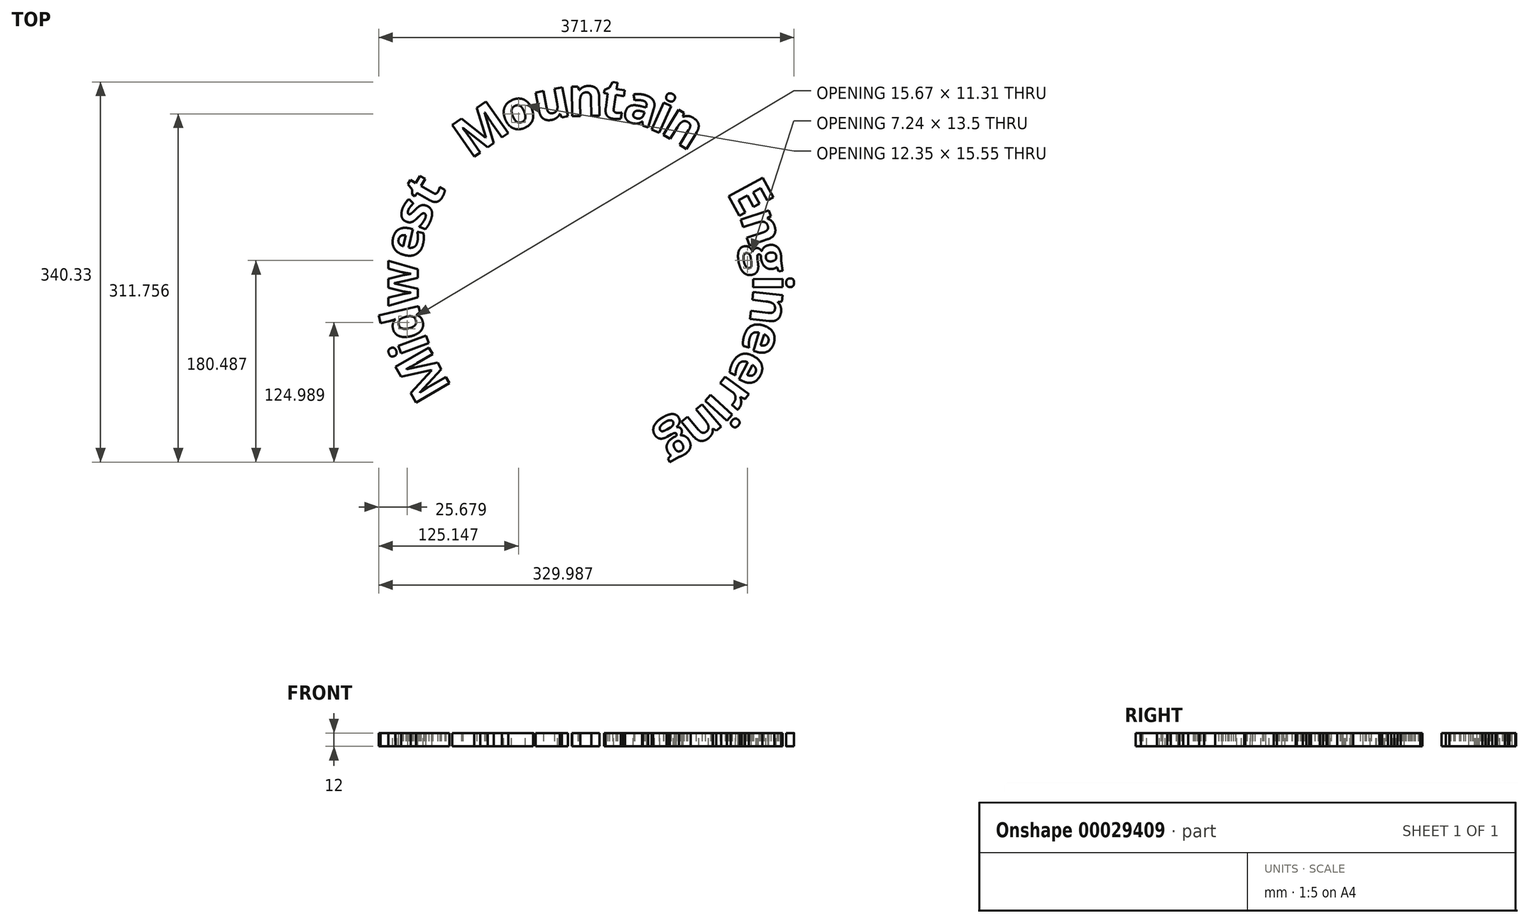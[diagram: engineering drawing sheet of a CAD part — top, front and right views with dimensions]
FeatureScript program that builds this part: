
annotation { "Feature Type Name" : "Feature", "Feature Type Description" : "" }
export const myFeature = defineFeature(function(context is Context, id is Id, definition is map)
    precondition{}
    {
        {
            var Q0;
            Q0=qCreatedBy(makeId("Top.planeOp"),FACE);
            var sketch = newSketch(context, id + "F0", { "sketchPlane" : qUnion([Q0])});
            skCircle(sketch, "E0", {"center": v(0, 0) * mm, "radius": 150 * mm, "construction": true});
            skLineSegment(sketch, "E1", {"start": v(0, 0) * mm, "end": v(-129.76, -75.25) * mm, "construction": true});
            skLineSegment(sketch, "E2", {"start": v(0, 0) * mm, "end": v(-140.83, -51.63) * mm, "construction": true});
            skLineSegment(sketch, "E3", {"start": v(0, 0) * mm, "end": v(-146.23, -33.4) * mm, "construction": true});
            skLineSegment(sketch, "E4", {"start": v(0, 0) * mm, "end": v(-150, 0) * mm, "construction": true});
            skLineSegment(sketch, "E5", {"start": v(0, 0) * mm, "end": v(-146.27, 33.23) * mm, "construction": true});
            skLineSegment(sketch, "E6", {"start": v(0, 0) * mm, "end": v(-139, 56.36) * mm, "construction": true});
            skLineSegment(sketch, "E7", {"start": v(0, 0) * mm, "end": v(-129.9, 75) * mm, "construction": true});
            skLineSegment(sketch, "E8", {"start": v(0, 0) * mm, "end": v(-86.04, 122.87) * mm, "construction": true});
            skLineSegment(sketch, "E9", {"start": v(0, 0) * mm, "end": v(-55.94, 139.18) * mm, "construction": true});
            skLineSegment(sketch, "E10", {"start": v(0, 0) * mm, "end": v(-29.36, 147.1) * mm, "construction": true});
            skLineSegment(sketch, "E11", {"start": v(0, 0) * mm, "end": v(-1.58, 150) * mm, "construction": true});
            skLineSegment(sketch, "E12", {"start": v(0, 0) * mm, "end": v(22.05, 148.37) * mm, "construction": true});
            skLineSegment(sketch, "E13", {"start": v(0, 0) * mm, "end": v(43.9, 143.43) * mm, "construction": true});
            skLineSegment(sketch, "E14", {"start": v(0, 0) * mm, "end": v(61.12, 136.98) * mm, "construction": true});
            skLineSegment(sketch, "E15", {"start": v(0, 0) * mm, "end": v(78.5, 127.82) * mm, "construction": true});
            skLineSegment(sketch, "E16", {"start": v(0, 0) * mm, "end": v(131.94, 71.35) * mm, "construction": true});
            skLineSegment(sketch, "E17", {"start": v(0, 0) * mm, "end": v(142.3, 47.44) * mm, "construction": true});
            skLineSegment(sketch, "E18", {"start": v(0, 0) * mm, "end": v(148.54, 20.85) * mm, "construction": true});
            skLineSegment(sketch, "E19", {"start": v(0, 0) * mm, "end": v(149.99, 1.95) * mm, "construction": true});
            skLineSegment(sketch, "E20", {"start": v(0, 0) * mm, "end": v(148.95, -17.68) * mm, "construction": true});
            skLineSegment(sketch, "E21", {"start": v(0, 0) * mm, "end": v(143.32, -44.26) * mm, "construction": true});
            skLineSegment(sketch, "E22", {"start": v(0, 0) * mm, "end": v(133.36, -68.67) * mm, "construction": true});
            skLineSegment(sketch, "E23", {"start": v(0, 0) * mm, "end": v(120.93, -88.75) * mm, "construction": true});
            skLineSegment(sketch, "E24", {"start": v(0, 0) * mm, "end": v(110.73, -101.19) * mm, "construction": true});
            skLineSegment(sketch, "E25", {"start": v(0, 0) * mm, "end": v(96.55, -114.8) * mm, "construction": true});
            skLineSegment(sketch, "E26", {"start": v(0, 0) * mm, "end": v(74.14, -130.4) * mm, "construction": true});
            skText(sketch, "E27", { "text": "M", "fontName": "OpenSans-Bold.ttf"});
            skText(sketch, "E28", { "text": "i", "fontName": "OpenSans-Bold.ttf"});
            skText(sketch, "E29", { "text": "d", "fontName": "OpenSans-Bold.ttf"});
            skText(sketch, "E30", { "text": "w", "fontName": "OpenSans-Bold.ttf"});
            skText(sketch, "E31", { "text": "e", "fontName": "OpenSans-Bold.ttf"});
            skText(sketch, "E32", { "text": "s", "fontName": "OpenSans-Bold.ttf"});
            skText(sketch, "E33", { "text": "t", "fontName": "OpenSans-Bold.ttf"});
            skText(sketch, "E34", { "text": "o", "fontName": "OpenSans-Bold.ttf"});
            skText(sketch, "E35", { "text": "u", "fontName": "OpenSans-Bold.ttf"});
            skText(sketch, "E36", { "text": "n", "fontName": "OpenSans-Bold.ttf"});
            skText(sketch, "E37", { "text": "M", "fontName": "OpenSans-Bold.ttf"});
            skText(sketch, "E38", { "text": "t", "fontName": "OpenSans-Bold.ttf"});
            skText(sketch, "E39", { "text": "a", "fontName": "OpenSans-Bold.ttf"});
            skText(sketch, "E40", { "text": "i", "fontName": "OpenSans-Bold.ttf"});
            skText(sketch, "E41", { "text": "n", "fontName": "OpenSans-Bold.ttf"});
            skText(sketch, "E42", { "text": "E", "fontName": "OpenSans-Bold.ttf"});
            skText(sketch, "E43", { "text": "n", "fontName": "OpenSans-Bold.ttf"});
            skText(sketch, "E44", { "text": "g", "fontName": "OpenSans-Bold.ttf"});
            skText(sketch, "E45", { "text": "i", "fontName": "OpenSans-Bold.ttf"});
            skText(sketch, "E46", { "text": "n", "fontName": "OpenSans-Bold.ttf"});
            skText(sketch, "E47", { "text": "e", "fontName": "OpenSans-Bold.ttf"});
            skText(sketch, "E48", { "text": "e", "fontName": "OpenSans-Bold.ttf"});
            skText(sketch, "E49", { "text": "r", "fontName": "OpenSans-Bold.ttf"});
            skText(sketch, "E50", { "text": "i", "fontName": "OpenSans-Bold.ttf"});
            skText(sketch, "E51", { "text": "n", "fontName": "OpenSans-Bold.ttf"});
            skText(sketch, "E52", { "text": "g", "fontName": "OpenSans-Bold.ttf"});
            skLineSegment(sketch, "E53", {"start": v(-69.16, 134.69) * mm, "end": v(0, 0) * mm, "construction": true});
            skLineSegment(sketch, "E54", {"start": v(-43.07, 144.35) * mm, "end": v(0, 0) * mm, "construction": true});
            skLineSegment(sketch, "E55", {"start": v(-15.64, 149.84) * mm, "end": v(0, 0) * mm, "construction": true});
            skLineSegment(sketch, "E56", {"start": v(12.47, 150.14) * mm, "end": v(0, 0) * mm, "construction": true});
            skLineSegment(sketch, "E57", {"start": v(31.65, 146.94) * mm, "end": v(0, 0) * mm, "construction": true});
            skLineSegment(sketch, "E58", {"start": v(56.12, 139.7) * mm, "end": v(0, 0) * mm, "construction": true});
            skLineSegment(sketch, "E59", {"start": v(66.28, 134.68) * mm, "end": v(0, 0) * mm, "construction": true});
            skLineSegment(sketch, "E60", {"start": v(0, 0) * mm, "end": v(150, 0) * mm, "construction": true});
            skLineSegment(sketch, "E61", {"start": v(0, 0) * mm, "end": v(137.7, 60.7) * mm, "construction": true});
            skLineSegment(sketch, "E62", {"start": v(146.75, 34.1) * mm, "end": v(0, 0) * mm, "construction": true});
            skLineSegment(sketch, "E63", {"start": v(150.4, 7.62) * mm, "end": v(0, 0) * mm, "construction": true});
            skLineSegment(sketch, "E64", {"start": v(150.06, -3.7) * mm, "end": v(0, 0) * mm, "construction": true});
            skLineSegment(sketch, "E65", {"start": v(147.3, -31.64) * mm, "end": v(0, 0) * mm, "construction": true});
            skLineSegment(sketch, "E66", {"start": v(139.42, -56.9) * mm, "end": v(0, 0) * mm, "construction": true});
            skLineSegment(sketch, "E67", {"start": v(127.3, -80.43) * mm, "end": v(0, 0) * mm, "construction": true});
            skLineSegment(sketch, "E68", {"start": v(114.74, -97.19) * mm, "end": v(0, 0) * mm, "construction": true});
            skLineSegment(sketch, "E69", {"start": v(106.92, -105.36) * mm, "end": v(0, 0) * mm, "construction": true});
            skLineSegment(sketch, "E70", {"start": v(85.8, -123.84) * mm, "end": v(0, 0) * mm, "construction": true});
            skLineSegment(sketch, "E71", {"start": v(-140.1, -57.43) * mm, "end": v(0, 0) * mm, "construction": true});
            skLineSegment(sketch, "E72", {"start": v(-142.78, -46.33) * mm, "end": v(0, 0) * mm, "construction": true});
            skLineSegment(sketch, "E73", {"start": v(-149.22, -20.33) * mm, "end": v(0, 0) * mm, "construction": true});
            skLineSegment(sketch, "E74", {"start": v(-150, 20.44) * mm, "end": v(0, 0) * mm, "construction": true});
            skLineSegment(sketch, "E75", {"start": v(-143.34, 46.14) * mm, "end": v(0, 0) * mm, "construction": true});
            skLineSegment(sketch, "E76", {"start": v(-134.84, 66.64) * mm, "end": v(0, 0) * mm, "construction": true});
            const initialGuessF0  = {"E27": [-0.11942, -0.09307, -0.50168, 0.86505, 0.03478], "E28": [-0.13889, -0.05694, -0.3442, 0.9389, 0.03478], "E29": [-0.14325, -0.04648, -0.2227, 0.97489, 0.03478], "E30": [-0.15, -0.02044, 0, 1, 0.03478], "E31": [-0.1492, 0.02033, 0.22156, 0.97515, 0.03478], "E32": [-0.14318, 0.04608, 0.37573, 0.92673, 0.03478], "E33": [-0.13476, 0.0666, 0.5, 0.86603, 0.03478], "E34": [-0.0688, 0.134, 0.92786, 0.37293, 0.03478], "E35": [-0.04307, 0.14436, 0.98066, 0.19572, 0.03478], "E36": [-0.01564, 0.14984, 0.99994, 0.01056, 0.03478], "E37": [-0.10291, 0.11106, 0.81915, 0.57358, 0.03478], "E38": [0.01244, 0.1498, 0.98914, -0.14697, 0.03478], "E39": [0.0317, 0.14717, 0.9562, -0.29272, 0.03478], "E40": [0.05596, 0.13929, 0.91323, -0.40744, 0.03478], "E41": [0.06652, 0.13518, 0.85213, -0.52332, 0.03478], "E42": [0.12619, 0.082, 0.47567, -0.87962, 0.03478], "E43": [0.13785, 0.06078, 0.31626, -0.94867, 0.03478], "E44": [0.14669, 0.03409, 0.13903, -0.99029, 0.03478], "E45": [0.14991, 0.0076, 0.01297, -0.99992, 0.03478], "E46": [0.15061, -0.00372, -0.11785, -0.99303, 0.03478], "E47": [0.14722, -0.03162, -0.2951, -0.95547, 0.03478], "E48": [0.13942, -0.0569, -0.4578, -0.88905, 0.03478], "E49": [0.12712, -0.08032, -0.59168, -0.80617, 0.03478], "E50": [0.11454, -0.09702, -0.6746, -0.73819, 0.03478], "E51": [0.1073, -0.10575, -0.7653, -0.64367, 0.03478], "E52": [0.08576, -0.1238, -0.86932, -0.49425, 0.03478]};
            skSetInitialGuess(sketch, initialGuessF0);
            skSolve(sketch);
        }
        {
            var Q0;
            Q0=qSketchRegion(id+"F0",true);
            extrude(context, id + "F1", {"entities" : qUnion([Q0]), "depth" : 10 * mm, "hasSecondDirection" : true, "secondDirectionOppositeDirection" : true, "secondDirectionDepth" : 2 * mm});
        }
    });
